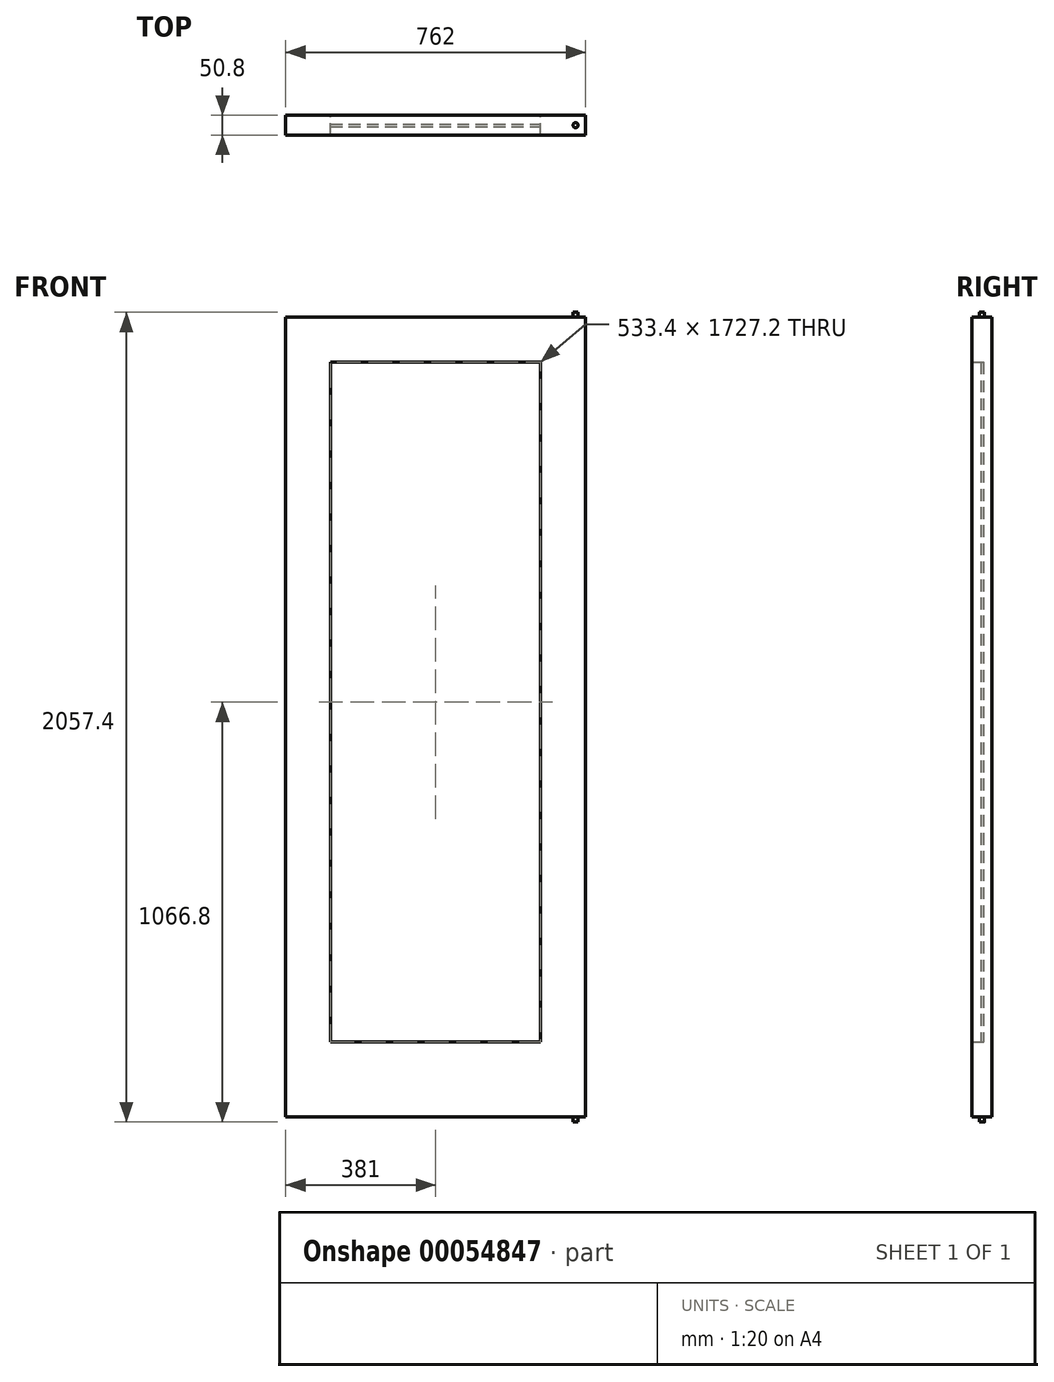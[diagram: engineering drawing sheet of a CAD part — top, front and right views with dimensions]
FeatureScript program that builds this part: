
annotation { "Feature Type Name" : "Feature", "Feature Type Description" : "" }
export const myFeature = defineFeature(function(context is Context, id is Id, definition is map)
    precondition{}
    {
        {
            var Q0;
            Q0=qCreatedBy(makeId("Front.planeOp"),FACE);
            var sketch = newSketch(context, id + "F0", { "sketchPlane" : qUnion([Q0])});
            skLineSegment(sketch, "E0.rect.bottom", {"start": v(381, 1016) * mm, "end": v(-381, 1016) * mm});
            skLineSegment(sketch, "E0.rect.top", {"start": v(381, -1016) * mm, "end": v(-381, -1016) * mm});
            skLineSegment(sketch, "E0.rect.left", {"start": v(381, 1016) * mm, "end": v(381, -1016) * mm});
            skLineSegment(sketch, "E0.rect.right", {"start": v(-381, 1016) * mm, "end": v(-381, -1016) * mm});
            skPoint(sketch, "E0.rect.middle", {"position": v(0, 0) * mm});
            skLineSegment(sketch, "E1.bottom", {"start": v(-266.7, 901.7) * mm, "end": v(266.7, 901.7) * mm});
            skLineSegment(sketch, "E1.top", {"start": v(-266.7, -825.5) * mm, "end": v(266.7, -825.5) * mm});
            skLineSegment(sketch, "E1.left", {"start": v(-266.7, 901.7) * mm, "end": v(-266.7, -825.5) * mm});
            skLineSegment(sketch, "E1.right", {"start": v(266.7, 901.7) * mm, "end": v(266.7, -825.5) * mm});
            skSolve(sketch);
        }
        {
            var Q0;
            Q0=makeQuery(id+"F0.imprint","IMPRINT",FACE,{"disambiguationData":[TD([[makeQuery(id+"F0.imprint","IMPRINT",EDGE,{"derivedFrom":sQuery(id+"F0.wireOp",EDGE,"E0.rect.bottom")}),1.0]])]});
            extrude(context, id + "F1", {"entities" : qUnion([Q0]), "depth" : 25.4 * mm, "hasSecondDirection" : true, "secondDirectionOppositeDirection" : true, "secondDirectionDepth" : 25.4 * mm});
        }
        {
            var Q0;
            Q0=makeQuery(id+"F0.imprint","IMPRINT",FACE,{"disambiguationData":[TD([[makeQuery(id+"F0.imprint","IMPRINT",EDGE,{"derivedFrom":sQuery(id+"F0.wireOp",EDGE,"E1.bottom")}),-1.0]])]});
            extrude(context, id + "F2", {"entities" : qUnion([Q0]), "depth" : 3.17 * mm, "hasSecondDirection" : true, "secondDirectionOppositeDirection" : true, "secondDirectionDepth" : 3.17 * mm});
        }
        {
            var Q0;
            Q0=makeQuery(id+"F1.opExtrude","SWEPT_FACE",FACE,{"disambiguationData":[OSD([sQuery(id+"F0.wireOp",EDGE,"E0.rect.bottom")])]});
            var sketch = newSketch(context, id + "F3", { "sketchPlane" : qUnion([Q0])});
            skLineSegment(sketch, "E2", {"start": v(381, 0) * mm, "end": v(355.6, 0) * mm, "construction": true});
            skCircle(sketch, "E3", {"center": v(355.6, 0) * mm, "radius": 6.35 * mm});
            skSolve(sketch);
        }
        {
            var Q0;
            Q0=qSketchRegion(id+"F3",true);
            extrude(context, id + "F4", {"entities" : qUnion([Q0]), "operationType" : NewBodyOperationType.ADD, "depth" : 12.7 * mm, "hasSecondDirection" : true, "secondDirectionOppositeDirection" : true, "secondDirectionDepth" : 2044.7 * mm});
        }
    });
